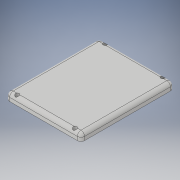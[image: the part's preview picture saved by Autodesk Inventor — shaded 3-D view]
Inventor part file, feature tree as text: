
AUTODESK INVENTOR PART (.ipt)
format: ipt  version: 2017 (Build 210142000, 142)  size: 138,240 bytes
history: native  units: in
note: dims shown in document units (in); Inventor stores cm internally (conversion verified against a paired STEP export)
features: extrude x2, fillet x2, sketch x2
ambient origin geometry x8: Origin, YZ Plane, XZ Plane, XY Plane, X Axis, Y Axis, Z Axis, Center Point
bodies: Solid1 (feature_tree)
feature tree (6):
  extrude  "Extrusion1"  Depth=3.225in
  fillet  "Fillet1"  Radius=0.25in
  fillet  "Fillet2"  Radius=0.125in
  extrude  "Extrusion2"  Depth=0.0938in
  sketch  "Sketch1"  dims[d0=2.6in d1=3.225in d2=0.25in d3=0.0in d4=0.125in]
  sketch  "Sketch2"  dims[d5=0.125in d6=0.0938in d7=0.1285in d8=1.0in d9=0.25in d10=0.0in]
